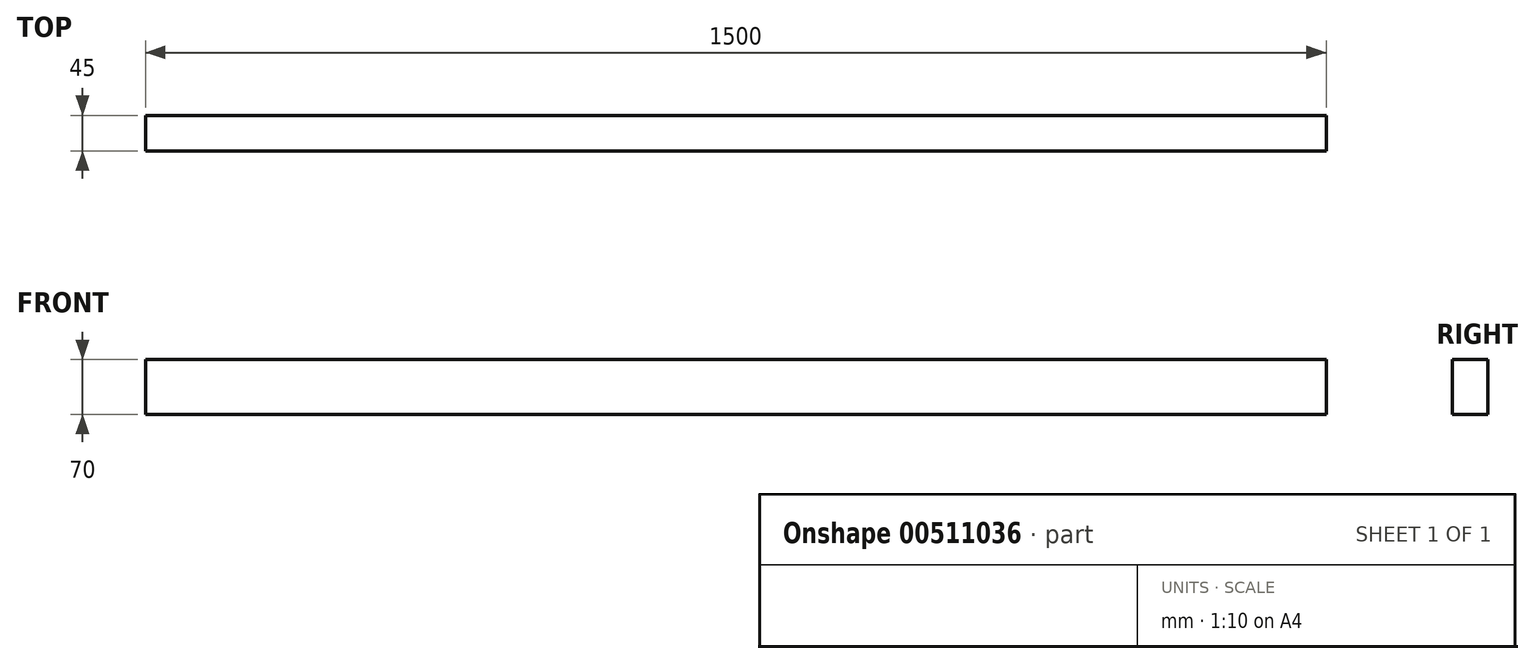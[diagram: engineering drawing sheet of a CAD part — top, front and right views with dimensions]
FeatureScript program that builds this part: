
annotation { "Feature Type Name" : "Feature", "Feature Type Description" : "" }
export const myFeature = defineFeature(function(context is Context, id is Id, definition is map)
    precondition{}
    {
        {
            var Q0;
            Q0=qCreatedBy(makeId("Front.planeOp"),FACE);
            var sketch = newSketch(context, id + "F0", { "sketchPlane" : qUnion([Q0])});
            skLineSegment(sketch, "E0.bottom", {"start": v(0, 0) * mm, "end": v(-1500, 0) * mm});
            skLineSegment(sketch, "E0.top", {"start": v(0, 70) * mm, "end": v(-1500, 70) * mm});
            skLineSegment(sketch, "E0.left", {"start": v(0, 0) * mm, "end": v(0, 70) * mm});
            skLineSegment(sketch, "E0.right", {"start": v(-1500, 0) * mm, "end": v(-1500, 70) * mm});
            skSolve(sketch);
        }
        {
            var Q0;
            Q0=qSketchRegion(id+"F0",true);
            extrude(context, id + "F1", {"entities" : qUnion([Q0]), "depth" : 45 * mm});
        }
    });
